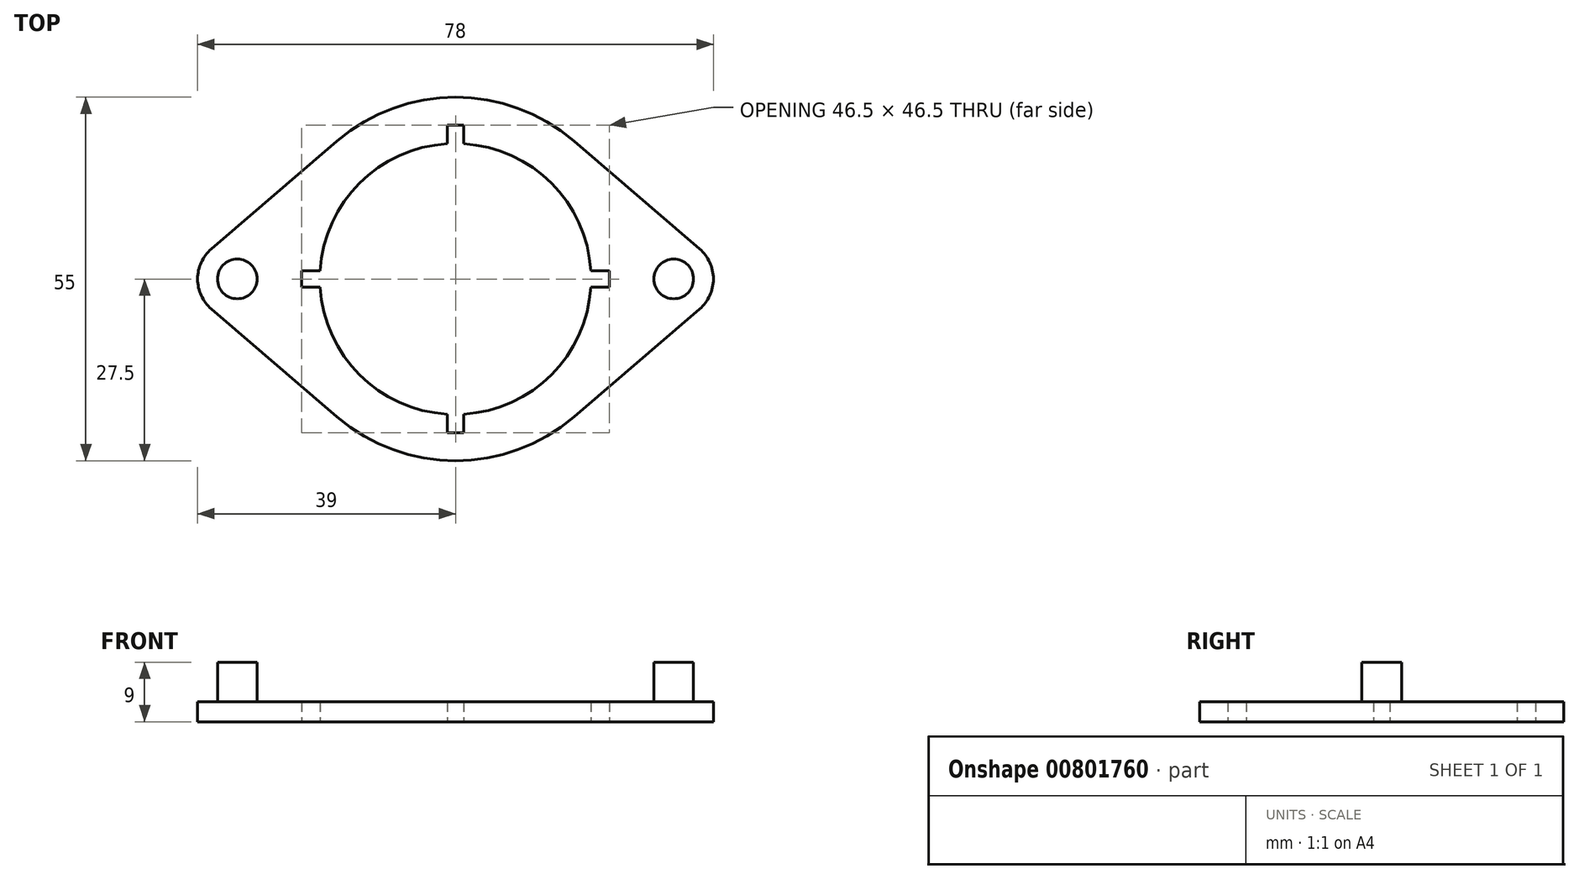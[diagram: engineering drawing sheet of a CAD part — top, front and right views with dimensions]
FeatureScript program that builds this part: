
annotation { "Feature Type Name" : "Feature", "Feature Type Description" : "" }
export const myFeature = defineFeature(function(context is Context, id is Id, definition is map)
    precondition{}
    {
        {
            var Q0;
            Q0=qCreatedBy(makeId("Top.planeOp"),FACE);
            var sketch = newSketch(context, id + "F0", { "sketchPlane" : qUnion([Q0])});
            skCircle(sketch, "E0", {"center": v(0, 0) * mm, "radius": 18.5 * mm});
            skPoint(sketch, "E1", {"position": v(-33, 0) * mm});
            skPoint(sketch, "E2", {"position": v(33, 0) * mm});
            skCircle(sketch, "E3", {"center": v(-33, 0) * mm, "radius": 3 * mm});
            skCircle(sketch, "E4", {"center": v(33, 0) * mm, "radius": 3 * mm});
            skCircle(sketch, "E5", {"center": v(0, 0) * mm, "radius": 27.5 * mm});
            skCircle(sketch, "E6", {"center": v(-33, 0) * mm, "radius": 6 * mm});
            skCircle(sketch, "E7", {"center": v(33, 0) * mm, "radius": 6 * mm});
            skLineSegment(sketch, "E8", {"start": v(-40.48, 1.49) * mm, "end": v(-8.54, 28.92) * mm});
            skLineSegment(sketch, "E9", {"start": v(9.11, 28.42) * mm, "end": v(40.24, 1.7) * mm});
            skLineSegment(sketch, "E10", {"start": v(-40.32, -1.62) * mm, "end": v(-10.2, -27.48) * mm});
            skLineSegment(sketch, "E11", {"start": v(40.01, -1.89) * mm, "end": v(10.26, -27.43) * mm});
            skCircle(sketch, "E12", {"center": v(0, 0) * mm, "radius": 20.5 * mm});
            skLineSegment(sketch, "E13.bottom", {"start": v(-1.25, 23.25) * mm, "end": v(1.25, 23.25) * mm});
            skLineSegment(sketch, "E13.top", {"start": v(-1.25, -23.25) * mm, "end": v(1.25, -23.25) * mm});
            skLineSegment(sketch, "E13.left", {"start": v(-1.25, 23.25) * mm, "end": v(-1.25, -23.25) * mm});
            skLineSegment(sketch, "E13.right", {"start": v(1.25, 23.25) * mm, "end": v(1.25, -23.25) * mm});
            skLineSegment(sketch, "E14.bottom", {"start": v(-23.25, 1.25) * mm, "end": v(23.25, 1.25) * mm});
            skLineSegment(sketch, "E14.top", {"start": v(-23.25, -1.25) * mm, "end": v(23.25, -1.25) * mm});
            skLineSegment(sketch, "E14.left", {"start": v(-23.25, 1.25) * mm, "end": v(-23.25, -1.25) * mm});
            skLineSegment(sketch, "E14.right", {"start": v(23.25, 1.25) * mm, "end": v(23.25, -1.25) * mm});
            skLineSegment(sketch, "E15.bottom", {"start": v(-3, 25) * mm, "end": v(3, 25) * mm});
            skLineSegment(sketch, "E15.top", {"start": v(-3, -25) * mm, "end": v(3, -25) * mm});
            skLineSegment(sketch, "E15.left", {"start": v(-3, 25) * mm, "end": v(-3, -25) * mm});
            skLineSegment(sketch, "E15.right", {"start": v(3, 25) * mm, "end": v(3, -25) * mm});
            skLineSegment(sketch, "E16.bottom", {"start": v(-25, 3) * mm, "end": v(25, 3) * mm});
            skLineSegment(sketch, "E16.top", {"start": v(-25, -3) * mm, "end": v(25, -3) * mm});
            skLineSegment(sketch, "E16.left", {"start": v(-25, 3) * mm, "end": v(-25, -3) * mm});
            skLineSegment(sketch, "E16.right", {"start": v(25, 3) * mm, "end": v(25, -3) * mm});
            skSolve(sketch);
        }
        {
            var Q0;
            {var subQ10=sQuery(id+"F0.wireOp",EDGE,"E15.bottom");Q0=makeQuery(id+"F0.imprint","IMPRINT",FACE,{"disambiguationData":[TD([[makeQuery(id+"F0.imprint","IMPRINT",EDGE,{"derivedFrom":subQ10}),1.0]])]});}
            var Q1;
            {var subQ0=sQuery(id+"F0.wireOp",EDGE,"E8");var subQ1=sQuery(id+"F0.wireOp",EDGE,"E5");var subQ2=makeQuery(id+"F0.imprint","INTERSECT",VERTEX,{"derivedFrom":[subQ1,subQ0]});Q1=makeQuery(id+"F0.imprint","IMPRINT",FACE,{"disambiguationData":[TD([[makeQuery(id+"F0.imprint","IMPRINT",EDGE,{"disambiguationData":[TD([[subQ2,-1.0]])],"derivedFrom":subQ1}),-1.0]])]});}
            var Q2;
            Q2=makeQuery(id+"F0.imprint","IMPRINT",FACE,{"disambiguationData":[TD([[makeQuery(id+"F0.imprint","IMPRINT",EDGE,{"derivedFrom":sQuery(id+"F0.wireOp",EDGE,"E3")}),-1.0]])]});
            var Q3;
            Q3=makeQuery(id+"F0.imprint","IMPRINT",FACE,{"disambiguationData":[TD([[makeQuery(id+"F0.imprint","IMPRINT",EDGE,{"derivedFrom":sQuery(id+"F0.wireOp",EDGE,"E3")}),1.0]])]});
            var Q4;
            {var subQ0=sQuery(id+"F0.wireOp",EDGE,"E10");var subQ1=sQuery(id+"F0.wireOp",EDGE,"E5");var subQ2=makeQuery(id+"F0.imprint","INTERSECT",VERTEX,{"derivedFrom":[subQ1,subQ0]});Q4=makeQuery(id+"F0.imprint","IMPRINT",FACE,{"disambiguationData":[TD([[makeQuery(id+"F0.imprint","IMPRINT",EDGE,{"disambiguationData":[TD([[subQ2,1.0]])],"derivedFrom":subQ1}),-1.0]])]});}
            var Q5;
            Q5=makeQuery(id+"F0.imprint","IMPRINT",FACE,{"disambiguationData":[TD([[makeQuery(id+"F0.imprint","IMPRINT",EDGE,{"derivedFrom":sQuery(id+"F0.wireOp",EDGE,"E4")}),-1.0]])]});
            var Q6;
            Q6=makeQuery(id+"F0.imprint","IMPRINT",FACE,{"disambiguationData":[TD([[makeQuery(id+"F0.imprint","IMPRINT",EDGE,{"derivedFrom":sQuery(id+"F0.wireOp",EDGE,"E4")}),1.0]])]});
            var Q7;
            {var subQ0=sQuery(id+"F0.wireOp",EDGE,"E11");var subQ1=sQuery(id+"F0.wireOp",EDGE,"E5");var subQ2=makeQuery(id+"F0.imprint","INTERSECT",VERTEX,{"derivedFrom":[subQ1,subQ0]});Q7=makeQuery(id+"F0.imprint","IMPRINT",FACE,{"disambiguationData":[TD([[makeQuery(id+"F0.imprint","IMPRINT",EDGE,{"disambiguationData":[TD([[subQ2,-1.0]])],"derivedFrom":subQ1}),-1.0]])]});}
            var Q8;
            {var subQ0=sQuery(id+"F0.wireOp",EDGE,"E9");var subQ1=sQuery(id+"F0.wireOp",EDGE,"E5");var subQ2=makeQuery(id+"F0.imprint","INTERSECT",VERTEX,{"derivedFrom":[subQ1,subQ0]});Q8=makeQuery(id+"F0.imprint","IMPRINT",FACE,{"disambiguationData":[TD([[makeQuery(id+"F0.imprint","IMPRINT",EDGE,{"disambiguationData":[TD([[subQ2,1.0]])],"derivedFrom":subQ1}),-1.0]])]});}
            var Q9;
            {var subQ0=sQuery(id+"F0.wireOp",EDGE,"E7");var subQ1=sQuery(id+"F0.wireOp",EDGE,"E5");var subQ2=makeQuery(id+"F0.imprint","INTERSECT",VERTEX,{"disambiguationData":[OD(0.0)],"derivedFrom":[subQ1,subQ0]});Q9=makeQuery(id+"F0.imprint","IMPRINT",FACE,{"disambiguationData":[TD([[makeQuery(id+"F0.imprint","IMPRINT",EDGE,{"disambiguationData":[TD([[subQ2,1.0]])],"derivedFrom":subQ1}),1.0]])]});}
            var Q10;
            {var subQ0=sQuery(id+"F0.wireOp",EDGE,"E6");var subQ1=sQuery(id+"F0.wireOp",EDGE,"E5");var subQ2=makeQuery(id+"F0.imprint","INTERSECT",VERTEX,{"disambiguationData":[OD(0.0)],"derivedFrom":[subQ1,subQ0]});Q10=makeQuery(id+"F0.imprint","IMPRINT",FACE,{"disambiguationData":[TD([[makeQuery(id+"F0.imprint","IMPRINT",EDGE,{"disambiguationData":[TD([[subQ2,-1.0]])],"derivedFrom":subQ1}),1.0]])]});}
            var Q11;
            {var subQ1=sQuery(id+"F0.wireOp",EDGE,"E13.bottom");Q11=makeQuery(id+"F0.imprint","IMPRINT",FACE,{"disambiguationData":[TD([[makeQuery(id+"F0.imprint","IMPRINT",EDGE,{"derivedFrom":subQ1}),1.0]])]});}
            var Q12;
            {var subQ0=sQuery(id+"F0.wireOp",EDGE,"E14.left");Q12=makeQuery(id+"F0.imprint","IMPRINT",FACE,{"disambiguationData":[TD([[makeQuery(id+"F0.imprint","IMPRINT",EDGE,{"derivedFrom":subQ0}),-1.0]])]});}
            var Q13;
            {var subQ1=sQuery(id+"F0.wireOp",EDGE,"E13.top");Q13=makeQuery(id+"F0.imprint","IMPRINT",FACE,{"disambiguationData":[TD([[makeQuery(id+"F0.imprint","IMPRINT",EDGE,{"derivedFrom":subQ1}),-1.0]])]});}
            var Q14;
            {var subQ0=sQuery(id+"F0.wireOp",EDGE,"E14.right");Q14=makeQuery(id+"F0.imprint","IMPRINT",FACE,{"disambiguationData":[TD([[makeQuery(id+"F0.imprint","IMPRINT",EDGE,{"derivedFrom":subQ0}),1.0]])]});}
            extrude(context, id + "F1", {"entities" : qUnion([Q0, Q1, Q2, Q3, Q4, Q5, Q6, Q7, Q8, Q9, Q10, Q11, Q12, Q13, Q14]), "depth" : 3 * mm, "offsetDistance" : 25 * mm});
        }
        {
            var Q0;
            Q0=makeQuery(id+"F0.imprint","IMPRINT",FACE,{"disambiguationData":[TD([[makeQuery(id+"F0.imprint","IMPRINT",EDGE,{"derivedFrom":sQuery(id+"F0.wireOp",EDGE,"E3")}),1.0]])]});
            var Q1;
            Q1=makeQuery(id+"F0.imprint","IMPRINT",FACE,{"disambiguationData":[TD([[makeQuery(id+"F0.imprint","IMPRINT",EDGE,{"derivedFrom":sQuery(id+"F0.wireOp",EDGE,"E4")}),1.0]])]});
            extrude(context, id + "F2", {"entities" : qUnion([Q0, Q1]), "operationType" : NewBodyOperationType.ADD, "depth" : 9 * mm, "offsetDistance" : 25 * mm});
        }
    });
